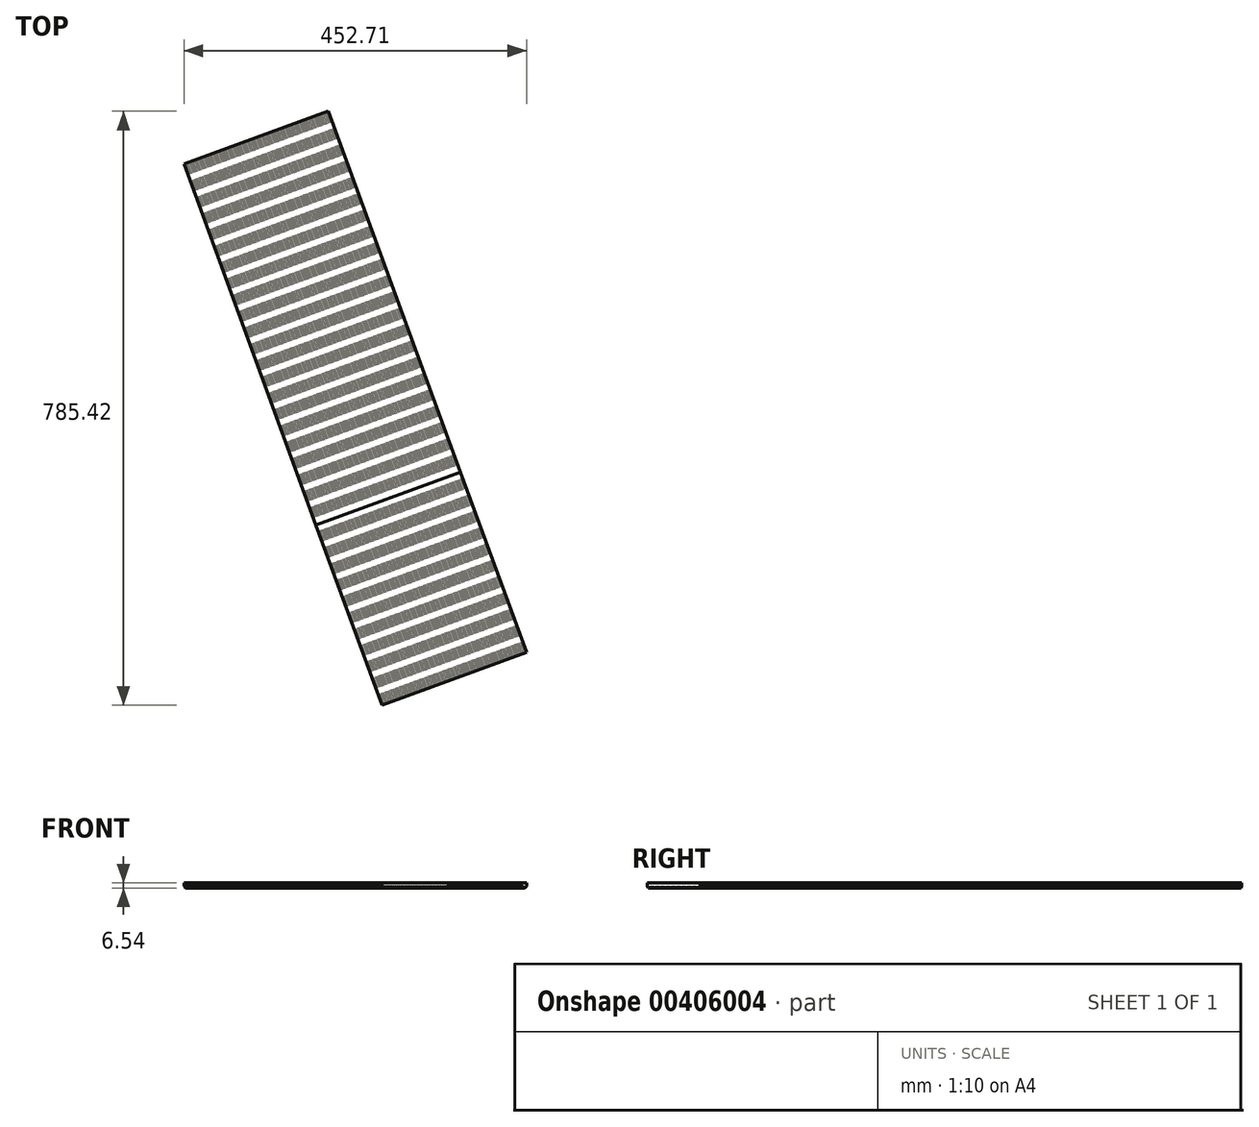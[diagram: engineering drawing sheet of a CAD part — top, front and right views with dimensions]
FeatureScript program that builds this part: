
annotation { "Feature Type Name" : "Feature", "Feature Type Description" : "" }
export const myFeature = defineFeature(function(context is Context, id is Id, definition is map)
    precondition{}
    {
        {
            var Q0;
            Q0=qCreatedBy(makeId("Top.planeOp"),FACE);
            var sketch = newSketch(context, id + "F0", { "sketchPlane" : qUnion([Q0])});
            skLineSegment(sketch, "E0", {"start": v(0, 0) * mm, "end": v(238.53, 87.3) * mm, "construction": true});
            skLineSegment(sketch, "E1", {"start": v(0, 0) * mm, "end": v(238.53, 0) * mm, "construction": true});
            skLineSegment(sketch, "E2", {"start": v(238.53, 87.3) * mm, "end": v(238.53, 0) * mm, "construction": true});
            skSolve(sketch);
        }
        {
            var Q0;
            Q0=sQuery(id+"F0.wireOp",EDGE,"E0");
            var Q1;
            Q1=qCreatedBy(makeId("Front.planeOp"),FACE);
            cPlane(context, id + "F1", {"entities" : qUnion([Q0, Q1]), "cplaneType" : CPlaneType.LINE_ANGLE, "offset" : 25.4 * mm, "angle" : 0 * degree, "width" : 152.4 * mm, "height" : 152.4 * mm});
        }
        {
            var Q0;
            Q0=qCreatedBy(id+"F1.planeOp",FACE);
            var sketch = newSketch(context, id + "F2", { "sketchPlane" : qUnion([Q0])});
            skLineSegment(sketch, "E3", {"start": v(0, 0) * mm, "end": v(-2.54, -2.54) * mm});
            skLineSegment(sketch, "E4", {"start": v(-2.54, -2.54) * mm, "end": v(-5.08, 0) * mm});
            skLineSegment(sketch, "E5", {"start": v(0, 0) * mm, "end": v(-5.08, 0) * mm, "construction": true});
            skLineSegment(sketch, "E6.1.0.0", {"start": v(-7.62, -2.54) * mm, "end": v(-10.16, 0) * mm});
            skLineSegment(sketch, "E6.1.0.1", {"start": v(-5.08, 0) * mm, "end": v(-7.62, -2.54) * mm});
            skLineSegment(sketch, "E6.1.0.2", {"start": v(-5.08, 0) * mm, "end": v(-10.16, 0) * mm, "construction": true});
            skLineSegment(sketch, "E6.2.0.0", {"start": v(-12.7, -2.54) * mm, "end": v(-15.24, 0) * mm});
            skLineSegment(sketch, "E6.2.0.1", {"start": v(-10.16, 0) * mm, "end": v(-12.7, -2.54) * mm});
            skLineSegment(sketch, "E6.2.0.2", {"start": v(-10.16, 0) * mm, "end": v(-15.24, 0) * mm, "construction": true});
            skLineSegment(sketch, "E6.direction1", {"start": v(-5.08, 0) * mm, "end": v(-10.16, 0) * mm, "construction": true});
            skLineSegment(sketch, "E7.0.3.0", {"start": v(-17.78, -2.54) * mm, "end": v(-20.32, 0) * mm});
            skLineSegment(sketch, "E7.3.3.0", {"start": v(-15.24, 0) * mm, "end": v(-17.78, -2.54) * mm});
            skLineSegment(sketch, "E7.6.3.0", {"start": v(-15.24, 0) * mm, "end": v(-20.32, 0) * mm, "construction": true});
            skLineSegment(sketch, "E7.0.4.0", {"start": v(-22.86, -2.54) * mm, "end": v(-25.4, 0) * mm});
            skLineSegment(sketch, "E7.3.4.0", {"start": v(-20.32, 0) * mm, "end": v(-22.86, -2.54) * mm});
            skLineSegment(sketch, "E7.6.4.0", {"start": v(-20.32, 0) * mm, "end": v(-25.4, 0) * mm, "construction": true});
            skLineSegment(sketch, "E7.0.5.0", {"start": v(-27.94, -2.54) * mm, "end": v(-30.48, 0) * mm});
            skLineSegment(sketch, "E7.3.5.0", {"start": v(-25.4, 0) * mm, "end": v(-27.94, -2.54) * mm});
            skLineSegment(sketch, "E7.6.5.0", {"start": v(-25.4, 0) * mm, "end": v(-30.48, 0) * mm, "construction": true});
            skLineSegment(sketch, "E7.0.6.0", {"start": v(-33.02, -2.54) * mm, "end": v(-35.56, 0) * mm});
            skLineSegment(sketch, "E7.3.6.0", {"start": v(-30.48, 0) * mm, "end": v(-33.02, -2.54) * mm});
            skLineSegment(sketch, "E7.6.6.0", {"start": v(-30.48, 0) * mm, "end": v(-35.56, 0) * mm, "construction": true});
            skLineSegment(sketch, "E7.0.7.0", {"start": v(-38.1, -2.54) * mm, "end": v(-40.64, 0) * mm});
            skLineSegment(sketch, "E7.3.7.0", {"start": v(-35.56, 0) * mm, "end": v(-38.1, -2.54) * mm});
            skLineSegment(sketch, "E7.6.7.0", {"start": v(-35.56, 0) * mm, "end": v(-40.64, 0) * mm, "construction": true});
            skLineSegment(sketch, "E7.0.8.0", {"start": v(-43.18, -2.54) * mm, "end": v(-45.72, 0) * mm});
            skLineSegment(sketch, "E7.3.8.0", {"start": v(-40.64, 0) * mm, "end": v(-43.18, -2.54) * mm});
            skLineSegment(sketch, "E7.6.8.0", {"start": v(-40.64, 0) * mm, "end": v(-45.72, 0) * mm, "construction": true});
            skLineSegment(sketch, "E7.0.9.0", {"start": v(-48.26, -2.54) * mm, "end": v(-50.8, 0) * mm});
            skLineSegment(sketch, "E7.3.9.0", {"start": v(-45.72, 0) * mm, "end": v(-48.26, -2.54) * mm});
            skLineSegment(sketch, "E7.6.9.0", {"start": v(-45.72, 0) * mm, "end": v(-50.8, 0) * mm, "construction": true});
            skLineSegment(sketch, "E7.0.10.0", {"start": v(-53.34, -2.54) * mm, "end": v(-55.88, 0) * mm});
            skLineSegment(sketch, "E7.3.10.0", {"start": v(-50.8, 0) * mm, "end": v(-53.34, -2.54) * mm});
            skLineSegment(sketch, "E7.6.10.0", {"start": v(-50.8, 0) * mm, "end": v(-55.88, 0) * mm, "construction": true});
            skLineSegment(sketch, "E7.0.11.0", {"start": v(-58.42, -2.54) * mm, "end": v(-60.96, 0) * mm});
            skLineSegment(sketch, "E7.3.11.0", {"start": v(-55.88, 0) * mm, "end": v(-58.42, -2.54) * mm});
            skLineSegment(sketch, "E7.6.11.0", {"start": v(-55.88, 0) * mm, "end": v(-60.96, 0) * mm, "construction": true});
            skLineSegment(sketch, "E7.0.12.0", {"start": v(-63.5, -2.54) * mm, "end": v(-66.04, 0) * mm});
            skLineSegment(sketch, "E7.3.12.0", {"start": v(-60.96, 0) * mm, "end": v(-63.5, -2.54) * mm});
            skLineSegment(sketch, "E7.6.12.0", {"start": v(-60.96, 0) * mm, "end": v(-66.04, 0) * mm, "construction": true});
            skLineSegment(sketch, "E7.0.13.0", {"start": v(-68.58, -2.54) * mm, "end": v(-71.12, 0) * mm});
            skLineSegment(sketch, "E7.3.13.0", {"start": v(-66.04, 0) * mm, "end": v(-68.58, -2.54) * mm});
            skLineSegment(sketch, "E7.6.13.0", {"start": v(-66.04, 0) * mm, "end": v(-71.12, 0) * mm, "construction": true});
            skLineSegment(sketch, "E7.0.14.0", {"start": v(-73.66, -2.54) * mm, "end": v(-76.2, 0) * mm});
            skLineSegment(sketch, "E7.3.14.0", {"start": v(-71.12, 0) * mm, "end": v(-73.66, -2.54) * mm});
            skLineSegment(sketch, "E7.6.14.0", {"start": v(-71.12, 0) * mm, "end": v(-76.2, 0) * mm, "construction": true});
            skLineSegment(sketch, "E7.0.15.0", {"start": v(-78.74, -2.54) * mm, "end": v(-81.28, 0) * mm});
            skLineSegment(sketch, "E7.3.15.0", {"start": v(-76.2, 0) * mm, "end": v(-78.74, -2.54) * mm});
            skLineSegment(sketch, "E7.6.15.0", {"start": v(-76.2, 0) * mm, "end": v(-81.28, 0) * mm, "construction": true});
            skLineSegment(sketch, "E7.0.16.0", {"start": v(-83.82, -2.54) * mm, "end": v(-86.36, 0) * mm});
            skLineSegment(sketch, "E7.3.16.0", {"start": v(-81.28, 0) * mm, "end": v(-83.82, -2.54) * mm});
            skLineSegment(sketch, "E7.6.16.0", {"start": v(-81.28, 0) * mm, "end": v(-86.36, 0) * mm, "construction": true});
            skLineSegment(sketch, "E7.0.17.0", {"start": v(-88.9, -2.54) * mm, "end": v(-91.44, 0) * mm});
            skLineSegment(sketch, "E7.3.17.0", {"start": v(-86.36, 0) * mm, "end": v(-88.9, -2.54) * mm});
            skLineSegment(sketch, "E7.6.17.0", {"start": v(-86.36, 0) * mm, "end": v(-91.44, 0) * mm, "construction": true});
            skLineSegment(sketch, "E7.0.18.0", {"start": v(-93.98, -2.54) * mm, "end": v(-96.52, 0) * mm});
            skLineSegment(sketch, "E7.3.18.0", {"start": v(-91.44, 0) * mm, "end": v(-93.98, -2.54) * mm});
            skLineSegment(sketch, "E7.6.18.0", {"start": v(-91.44, 0) * mm, "end": v(-96.52, 0) * mm, "construction": true});
            skLineSegment(sketch, "E7.0.19.0", {"start": v(-99.06, -2.54) * mm, "end": v(-101.6, 0) * mm});
            skLineSegment(sketch, "E7.3.19.0", {"start": v(-96.52, 0) * mm, "end": v(-99.06, -2.54) * mm});
            skLineSegment(sketch, "E7.6.19.0", {"start": v(-96.52, 0) * mm, "end": v(-101.6, 0) * mm, "construction": true});
            skLineSegment(sketch, "E7.0.20.0", {"start": v(-104.14, -2.54) * mm, "end": v(-106.68, 0) * mm});
            skLineSegment(sketch, "E7.3.20.0", {"start": v(-101.6, 0) * mm, "end": v(-104.14, -2.54) * mm});
            skLineSegment(sketch, "E7.6.20.0", {"start": v(-101.6, 0) * mm, "end": v(-106.68, 0) * mm, "construction": true});
            skLineSegment(sketch, "E7.0.21.0", {"start": v(-109.22, -2.54) * mm, "end": v(-111.76, 0) * mm});
            skLineSegment(sketch, "E7.3.21.0", {"start": v(-106.68, 0) * mm, "end": v(-109.22, -2.54) * mm});
            skLineSegment(sketch, "E7.6.21.0", {"start": v(-106.68, 0) * mm, "end": v(-111.76, 0) * mm, "construction": true});
            skLineSegment(sketch, "E7.0.22.0", {"start": v(-114.3, -2.54) * mm, "end": v(-116.84, 0) * mm});
            skLineSegment(sketch, "E7.3.22.0", {"start": v(-111.76, 0) * mm, "end": v(-114.3, -2.54) * mm});
            skLineSegment(sketch, "E7.6.22.0", {"start": v(-111.76, 0) * mm, "end": v(-116.84, 0) * mm, "construction": true});
            skLineSegment(sketch, "E7.0.23.0", {"start": v(-119.38, -2.54) * mm, "end": v(-121.92, 0) * mm});
            skLineSegment(sketch, "E7.3.23.0", {"start": v(-116.84, 0) * mm, "end": v(-119.38, -2.54) * mm});
            skLineSegment(sketch, "E7.6.23.0", {"start": v(-116.84, 0) * mm, "end": v(-121.92, 0) * mm, "construction": true});
            skLineSegment(sketch, "E7.0.24.0", {"start": v(-124.46, -2.54) * mm, "end": v(-127, 0) * mm});
            skLineSegment(sketch, "E7.3.24.0", {"start": v(-121.92, 0) * mm, "end": v(-124.46, -2.54) * mm});
            skLineSegment(sketch, "E7.6.24.0", {"start": v(-121.92, 0) * mm, "end": v(-127, 0) * mm, "construction": true});
            skLineSegment(sketch, "E7.0.25.0", {"start": v(-129.54, -2.54) * mm, "end": v(-132.08, 0) * mm});
            skLineSegment(sketch, "E7.3.25.0", {"start": v(-127, 0) * mm, "end": v(-129.54, -2.54) * mm});
            skLineSegment(sketch, "E7.6.25.0", {"start": v(-127, 0) * mm, "end": v(-132.08, 0) * mm, "construction": true});
            skLineSegment(sketch, "E7.0.26.0", {"start": v(-134.62, -2.54) * mm, "end": v(-137.16, 0) * mm});
            skLineSegment(sketch, "E7.3.26.0", {"start": v(-132.08, 0) * mm, "end": v(-134.62, -2.54) * mm});
            skLineSegment(sketch, "E7.6.26.0", {"start": v(-132.08, 0) * mm, "end": v(-137.16, 0) * mm, "construction": true});
            skLineSegment(sketch, "E7.0.27.0", {"start": v(-139.7, -2.54) * mm, "end": v(-142.24, 0) * mm});
            skLineSegment(sketch, "E7.3.27.0", {"start": v(-137.16, 0) * mm, "end": v(-139.7, -2.54) * mm});
            skLineSegment(sketch, "E7.6.27.0", {"start": v(-137.16, 0) * mm, "end": v(-142.24, 0) * mm, "construction": true});
            skLineSegment(sketch, "E7.0.28.0", {"start": v(-144.78, -2.54) * mm, "end": v(-147.32, 0) * mm});
            skLineSegment(sketch, "E7.3.28.0", {"start": v(-142.24, 0) * mm, "end": v(-144.78, -2.54) * mm});
            skLineSegment(sketch, "E7.6.28.0", {"start": v(-142.24, 0) * mm, "end": v(-147.32, 0) * mm, "construction": true});
            skLineSegment(sketch, "E7.0.29.0", {"start": v(-149.86, -2.54) * mm, "end": v(-152.4, 0) * mm});
            skLineSegment(sketch, "E7.3.29.0", {"start": v(-147.32, 0) * mm, "end": v(-149.86, -2.54) * mm});
            skLineSegment(sketch, "E7.6.29.0", {"start": v(-147.32, 0) * mm, "end": v(-152.4, 0) * mm, "construction": true});
            skLineSegment(sketch, "E7.0.30.0", {"start": v(-154.94, -2.54) * mm, "end": v(-157.48, 0) * mm});
            skLineSegment(sketch, "E7.3.30.0", {"start": v(-152.4, 0) * mm, "end": v(-154.94, -2.54) * mm});
            skLineSegment(sketch, "E7.6.30.0", {"start": v(-152.4, 0) * mm, "end": v(-157.48, 0) * mm, "construction": true});
            skLineSegment(sketch, "E7.0.31.0", {"start": v(-160.02, -2.54) * mm, "end": v(-162.56, 0) * mm});
            skLineSegment(sketch, "E7.3.31.0", {"start": v(-157.48, 0) * mm, "end": v(-160.02, -2.54) * mm});
            skLineSegment(sketch, "E7.6.31.0", {"start": v(-157.48, 0) * mm, "end": v(-162.56, 0) * mm, "construction": true});
            skLineSegment(sketch, "E7.0.32.0", {"start": v(-165.1, -2.54) * mm, "end": v(-167.64, 0) * mm});
            skLineSegment(sketch, "E7.3.32.0", {"start": v(-162.56, 0) * mm, "end": v(-165.1, -2.54) * mm});
            skLineSegment(sketch, "E7.6.32.0", {"start": v(-162.56, 0) * mm, "end": v(-167.64, 0) * mm, "construction": true});
            skLineSegment(sketch, "E7.0.33.0", {"start": v(-170.18, -2.54) * mm, "end": v(-172.72, 0) * mm});
            skLineSegment(sketch, "E7.3.33.0", {"start": v(-167.64, 0) * mm, "end": v(-170.18, -2.54) * mm});
            skLineSegment(sketch, "E7.6.33.0", {"start": v(-167.64, 0) * mm, "end": v(-172.72, 0) * mm, "construction": true});
            skLineSegment(sketch, "E7.0.34.0", {"start": v(-175.26, -2.54) * mm, "end": v(-177.8, 0) * mm});
            skLineSegment(sketch, "E7.3.34.0", {"start": v(-172.72, 0) * mm, "end": v(-175.26, -2.54) * mm});
            skLineSegment(sketch, "E7.6.34.0", {"start": v(-172.72, 0) * mm, "end": v(-177.8, 0) * mm, "construction": true});
            skLineSegment(sketch, "E7.0.35.0", {"start": v(-180.34, -2.54) * mm, "end": v(-182.88, 0) * mm});
            skLineSegment(sketch, "E7.3.35.0", {"start": v(-177.8, 0) * mm, "end": v(-180.34, -2.54) * mm});
            skLineSegment(sketch, "E7.6.35.0", {"start": v(-177.8, 0) * mm, "end": v(-182.88, 0) * mm, "construction": true});
            skLineSegment(sketch, "E7.0.36.0", {"start": v(-185.42, -2.54) * mm, "end": v(-187.96, 0) * mm});
            skLineSegment(sketch, "E7.3.36.0", {"start": v(-182.88, 0) * mm, "end": v(-185.42, -2.54) * mm});
            skLineSegment(sketch, "E7.6.36.0", {"start": v(-182.88, 0) * mm, "end": v(-187.96, 0) * mm, "construction": true});
            skLineSegment(sketch, "E7.0.37.0", {"start": v(-190.5, -2.54) * mm, "end": v(-193.04, 0) * mm});
            skLineSegment(sketch, "E7.3.37.0", {"start": v(-187.96, 0) * mm, "end": v(-190.5, -2.54) * mm});
            skLineSegment(sketch, "E7.6.37.0", {"start": v(-187.96, 0) * mm, "end": v(-193.04, 0) * mm, "construction": true});
            skLineSegment(sketch, "E7.0.38.0", {"start": v(-195.58, -2.54) * mm, "end": v(-198.12, 0) * mm});
            skLineSegment(sketch, "E7.3.38.0", {"start": v(-193.04, 0) * mm, "end": v(-195.58, -2.54) * mm});
            skLineSegment(sketch, "E7.6.38.0", {"start": v(-193.04, 0) * mm, "end": v(-198.12, 0) * mm, "construction": true});
            skLineSegment(sketch, "E7.0.39.0", {"start": v(-200.66, -2.54) * mm, "end": v(-203.2, 0) * mm});
            skLineSegment(sketch, "E7.3.39.0", {"start": v(-198.12, 0) * mm, "end": v(-200.66, -2.54) * mm});
            skLineSegment(sketch, "E7.6.39.0", {"start": v(-198.12, 0) * mm, "end": v(-203.2, 0) * mm, "construction": true});
            skLineSegment(sketch, "E8", {"start": v(0, 0) * mm, "end": v(0, 4) * mm});
            skLineSegment(sketch, "E9", {"start": v(0, 4) * mm, "end": v(-203.2, 4) * mm});
            skLineSegment(sketch, "E10", {"start": v(-203.2, 4) * mm, "end": v(-203.2, 0) * mm});
            skSolve(sketch);
        }
        {
            var Q0;
            Q0 = qSketchRegion(id + "F2", true);
            extrude(context, id + "F3", {"entities" : qUnion([Q0]), "oppositeDirection" : true, "depth" : 254 * mm});
        }
        {
            var Q0;
            Q0 = qSketchRegion(id + "F2", true);
            extrude(context, id + "F4", {"entities" : qUnion([Q0]), "depth" : 508 * mm});
        }
    });
